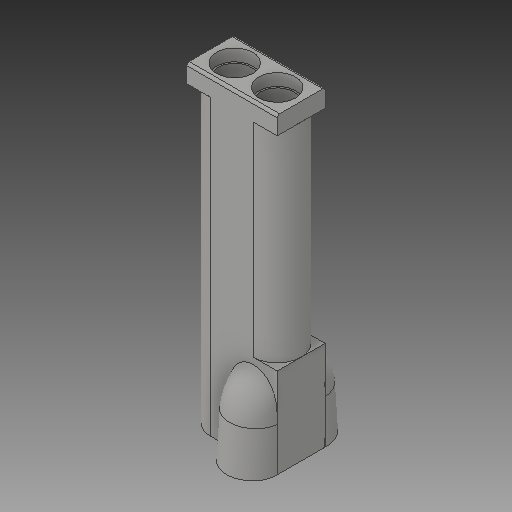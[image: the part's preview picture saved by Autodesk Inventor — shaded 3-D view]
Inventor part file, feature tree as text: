
AUTODESK INVENTOR PART (.ipt)
format: ipt  version: 2019 (Build 230136000, 136)  size: 205,824 bytes
history: native  units: in
note: dims shown in document units (in); Inventor stores cm internally (conversion verified against a paired STEP export)
features: other x3, sketch x1
ambient origin geometry x8: Origin, YZ Plane, XZ Plane, XY Plane, X Axis, Y Axis, Z Axis, Center Point
bodies: Solid1 (feature_tree)
feature tree (4):
  other  "in_syring_mixer_8.ipt"
  sketch  "Sketch1"  dims[d0=0.3937in]
  other  "mixer_cover::in_syring_mixer_8.ipt"
  other  "TaggingFeature1"
